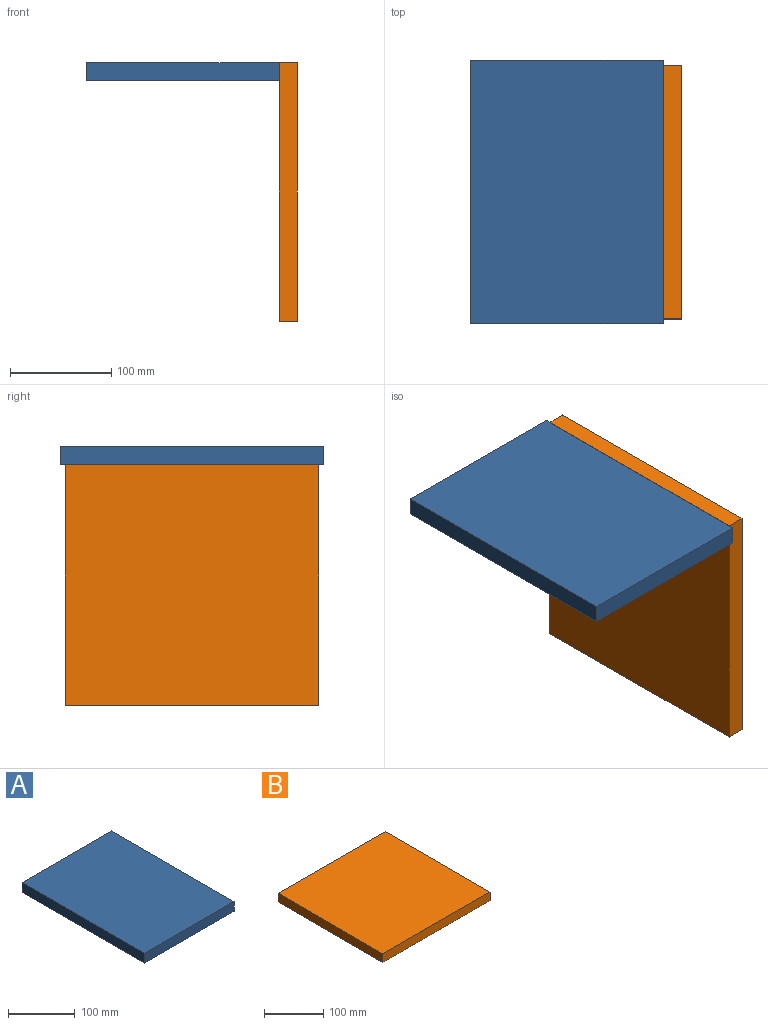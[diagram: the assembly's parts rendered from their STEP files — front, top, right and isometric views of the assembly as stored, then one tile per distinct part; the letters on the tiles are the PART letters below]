
ASSEMBLY  parts=2 mates=1
PART A: 6 faces, bbox 190x260x18 mm
  f0: plane 260x18mm, normal (-1,0,0), area 4680mm2, adj f1,f3,f4,f5
  f1: plane 190x18mm, normal (0,-1,0), area 3420mm2, adj f0,f2,f4,f5
  f2: plane 260x18mm, normal (1,0,0), area 4680mm2, adj f1,f3,f4,f5
  f3: plane 190x18mm, normal (0,1,0), area 3420mm2, adj f0,f2,f4,f5
  f4: plane 260x190mm, normal (0,0,1), area 49400mm2, adj f0,f1,f2,f3
  f5: plane 260x190mm, normal (0,0,-1), area 49400mm2, adj f0,f1,f2,f3
PART B: 6 faces, bbox 255x250x18 mm
  f0: plane 250x18mm, normal (-1,0,0), area 4500mm2, adj f1,f3,f4,f5
  f1: plane 255x18mm, normal (0,-1,0), area 4590mm2, adj f0,f2,f4,f5
  f2: plane 250x18mm, normal (1,0,0), area 4500mm2, adj f1,f3,f4,f5
  f3: plane 255x18mm, normal (0,1,0), area 4590mm2, adj f0,f2,f4,f5
  f4: plane 255x250mm, normal (0,0,1), area 63750mm2, adj f0,f1,f2,f3
  f5: plane 255x250mm, normal (0,0,-1), area 63750mm2, adj f0,f1,f2,f3
PLACE A t=(0,-70,0)mm
PLACE B rot(axis=(0,-1,0),90deg) t=(208,-65,-237)mm
MATE fastened B.f2 <-> A.f4  axis (0,0,1) through (190,60,18)mm
